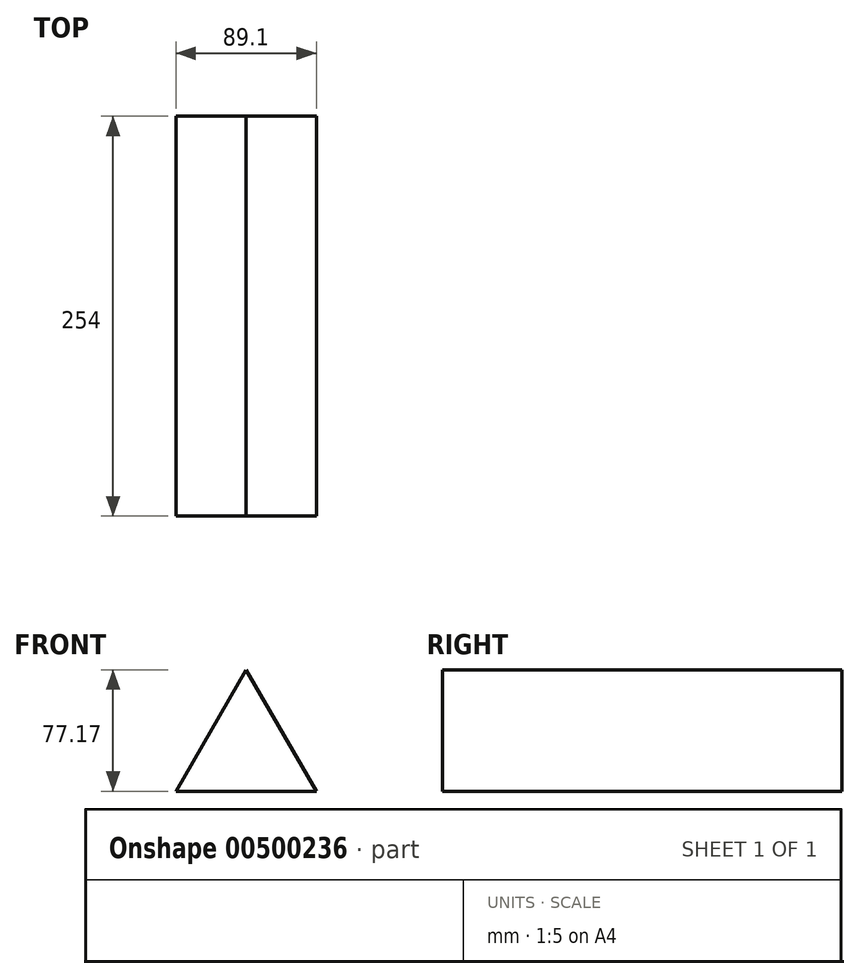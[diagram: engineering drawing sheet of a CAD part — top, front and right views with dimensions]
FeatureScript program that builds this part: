
annotation { "Feature Type Name" : "Feature", "Feature Type Description" : "" }
export const myFeature = defineFeature(function(context is Context, id is Id, definition is map)
    precondition{}
    {
        {
            var Q0;
            Q0=qCreatedBy(makeId("Front.planeOp"),FACE);
            var sketch = newSketch(context, id + "F0", { "sketchPlane" : qUnion([Q0])});
            skCircle(sketch, "E0.cCircle", {"center": v(0, 0) * mm, "radius": 51.45 * mm, "construction": true});
            skLineSegment(sketch, "E0.0", {"start": v(-44.55, -25.72) * mm, "end": v(0, 51.45) * mm});
            skLineSegment(sketch, "E0.1", {"start": v(0, 51.45) * mm, "end": v(44.55, -25.72) * mm});
            skLineSegment(sketch, "E0.2", {"start": v(44.55, -25.72) * mm, "end": v(-44.55, -25.72) * mm});
            skSolve(sketch);
        }
        {
            var Q0;
            Q0=makeQuery(id+"F0.imprint","IMPRINT",FACE,{"disambiguationData":[TD([[makeQuery(id+"F0.imprint","IMPRINT",EDGE,{"derivedFrom":sQuery(id+"F0.wireOp",EDGE,"E0.0")}),-1.0]])]});
            extrude(context, id + "F1", {"entities" : qUnion([Q0]), "endBound" : BoundingType.SYMMETRIC, "depth" : 254 * mm});
        }
    });
